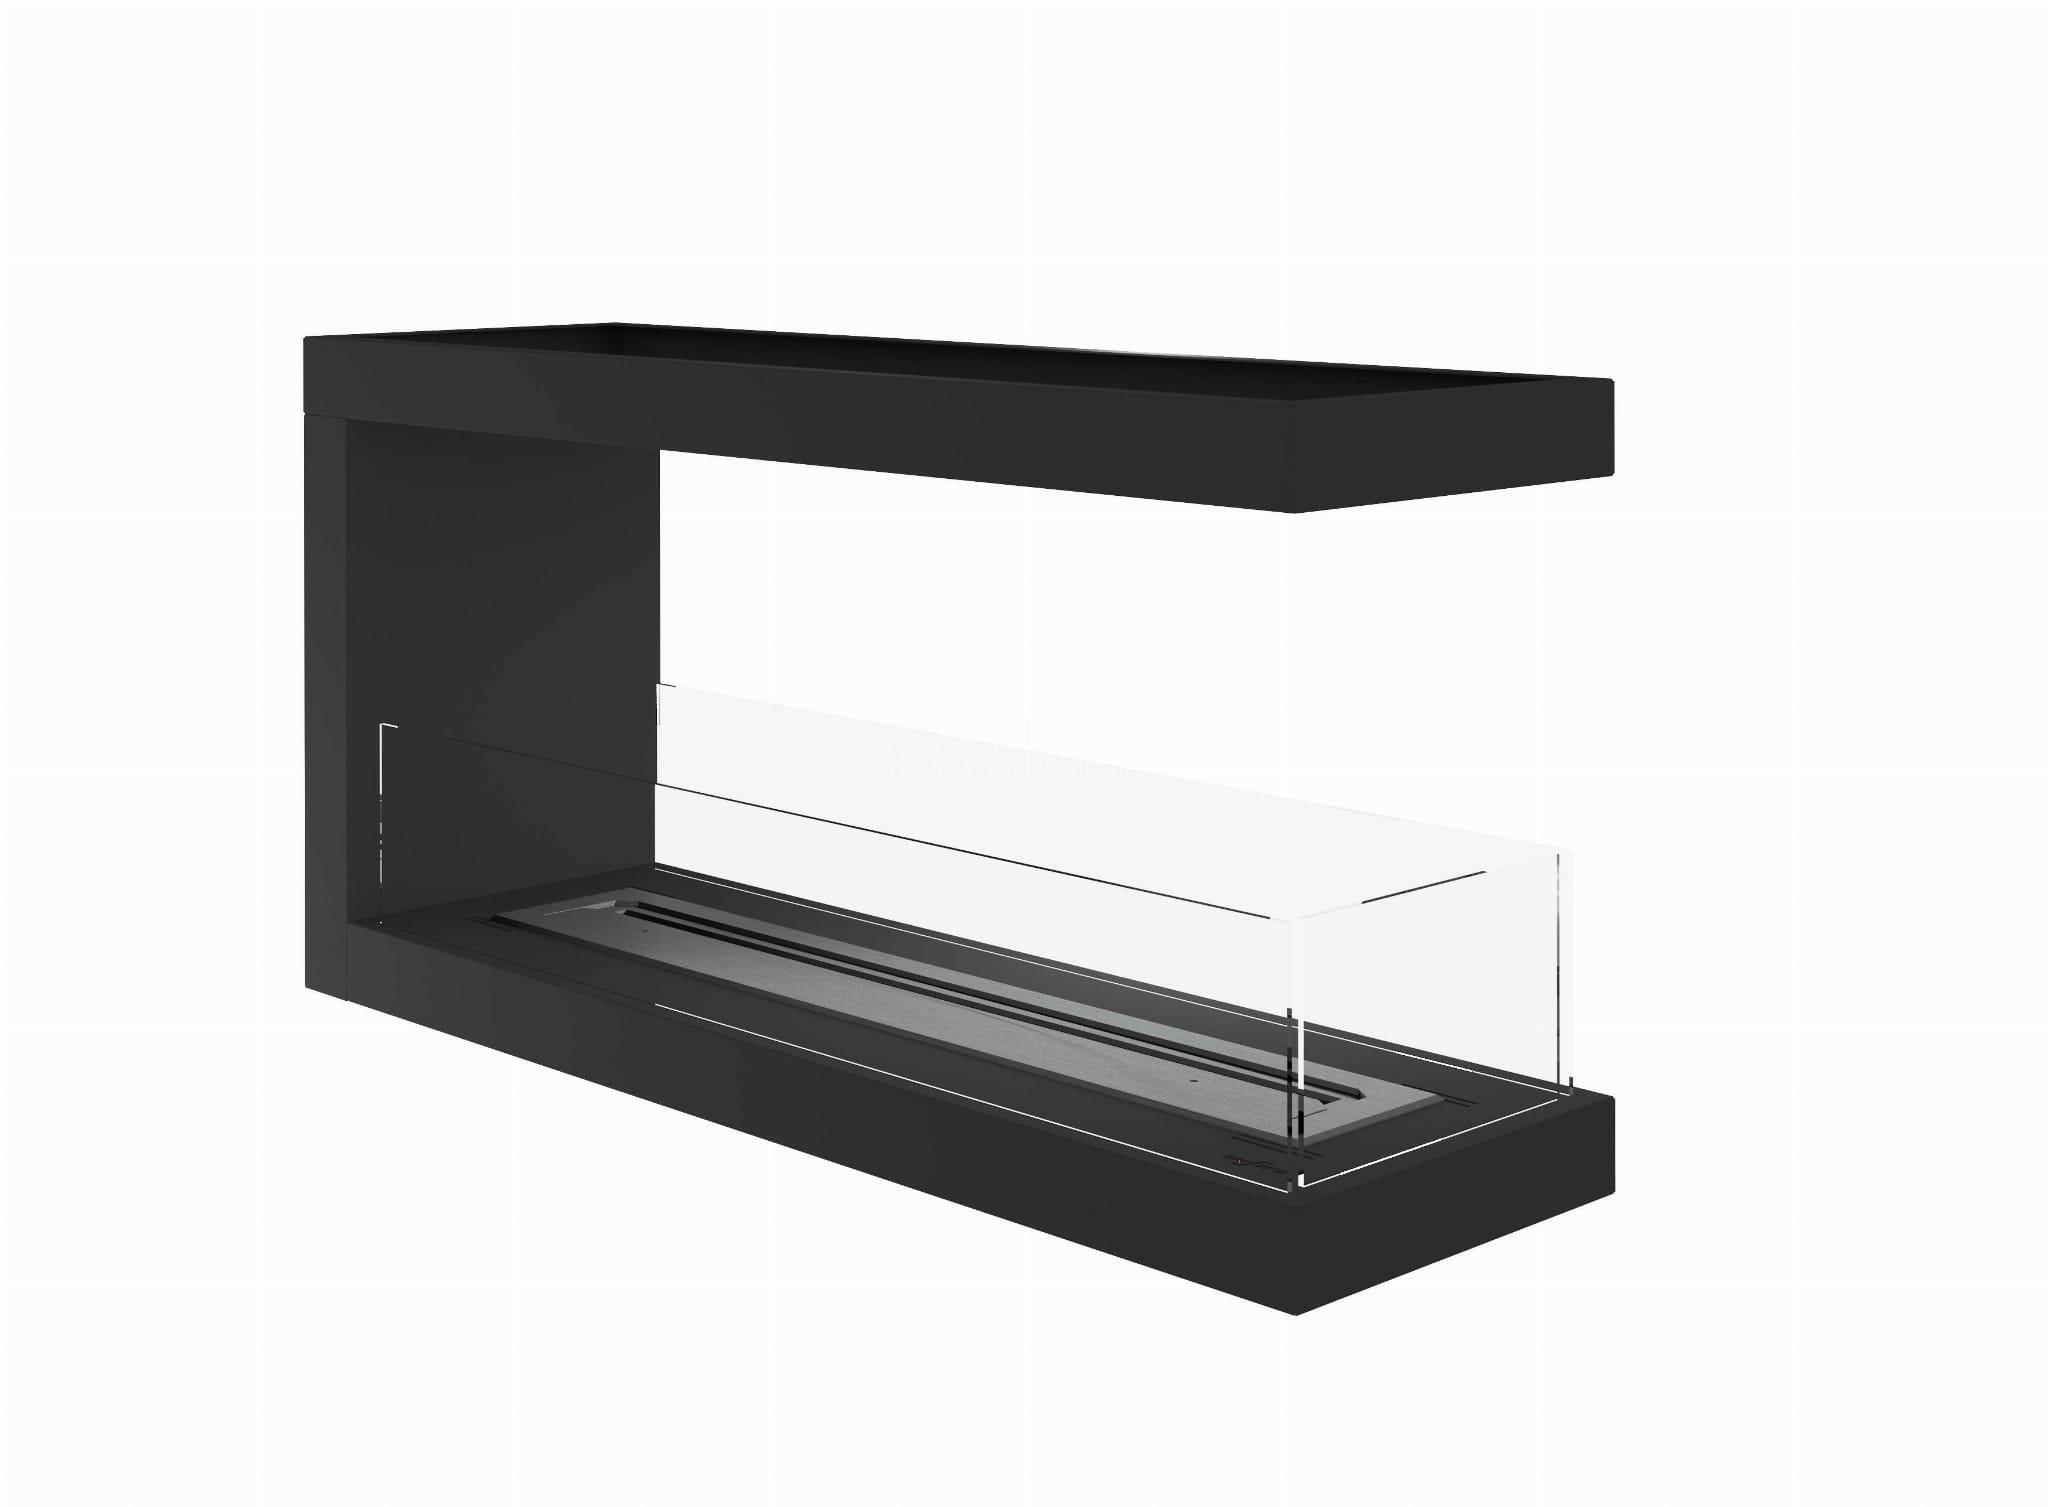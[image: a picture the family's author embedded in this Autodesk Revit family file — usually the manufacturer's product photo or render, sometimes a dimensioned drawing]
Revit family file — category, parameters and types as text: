
# Revit family: Infire_Inside U1000.1 .2
name_source: partatom
category: Zabudowa
revit_build: Autodesk Revit 2018 (Build: 20180329_1100(x64)
units: mm (PartAtom-declared; Revit-internal decimal feet)

## family parameters
Numer OmniClass = 23.40.20.34.14
Obiekt nadrzędny = Powierzchnia
Punkt obliczania pomieszczeń = Nie
Tnij formami wycięć po wczytaniu = Nie
Tytuł OmniClass = Fireplaces
Współdzielony = Nie

## types (2) — shared parameters
Domyślna rzędna = 1000 mm  [stored 3.28084 ft]
Gwarancja = 24 miesiące
Głębokość = 300 mm  [stored 0.984252 ft]
IfcExportAs = IfcSpaceHeaterType
Komentarze do typu = Biokominek
Materiał (obudowa) = INFIRE - czarny
Materiał (szkło) = INFIRE - szkło
Model = INSIDE U1000.1/U1000.2
Obraz typu = Insert_Inside U1000.2.jpg
Producent = INFIRE Biokominki
Szerokość = 1000 mm  [stored 3.28084 ft]
Szerokość szyby = 900 mm  [stored 2.95276 ft]
URL = http://www.infire.pl
Wysokość = 500 mm  [stored 1.64042 ft]
Wysokość szyby = 150 mm  [stored 0.492126 ft]

## per-type parameters (varying)
| type | Szkło | U1000.1 | U1000.2 |
| INSIDE U1000.2 | Szyba hartowana 4 mm, przyciemniana | Nie | Tak |
| INSIDE U1000.1 | Szyba hartowana 4 mm, przeźroczysta | Tak | Nie |

note: [stored X ft] marks values corroborated as IEEE doubles in the binary element streams (Revit-internal decimal feet)
